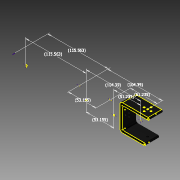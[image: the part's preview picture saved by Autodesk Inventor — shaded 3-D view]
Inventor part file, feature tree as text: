
AUTODESK INVENTOR PART (.ipt)
format: ipt  version: 2014 SP2 (Build 180246200, 246)  size: 362,496 bytes
history: native  units: in
note: dims shown in document units (in); Inventor stores cm internally (conversion verified against a paired STEP export)
features: sketch x18, extrude x13, reference x7, projected_geometry x5, mirror x4, pattern_circular x3, fillet x3, plane x2
ambient origin geometry x8: Origin, YZ Plane, XZ Plane, XY Plane, X Axis, Y Axis, Z Axis, Center Point
bodies: Solid1 (feature_tree)
feature tree (55):
  extrude  "Extrusion1"  Depth=0.1181in
  mirror  "Mirror1"
  mirror  "Mirror2"
  extrude  "Extrusion4"  Depth=2.126in
  mirror  "Mirror3"
  extrude  "Extrusion11"  Depth=0.1969in TaperAngle=0.0deg
  extrude  "Extrusion13"  Depth=0.0787in
  mirror  "Mirror4"
  extrude  "Extrusion14"  Depth=0.3937in
  pattern_circular  "Circular Pattern6"  Count=4 Angle=360.0deg
  extrude  "Extrusion15"  Depth=0.6299in
  pattern_circular  "Circular Pattern7"  Count=4 Angle=360.0deg
  extrude  "Extrusion16"  Depth=0.0787in
  plane  "Work Plane1"
  extrude  "Extrusion17"  Depth=0.1575in
  plane  "Work Plane3"
  extrude  "Extrusion18"  Depth=0.1181in
  sketch  "Sketch24"  dims[d78=0.5118in d79=0.6299in]
  extrude  "Extrusion22"  Depth=0.0591in
  sketch  "Sketch25"  dims[d80=0.1181in]
  extrude  "Extrusion23"  Depth=1.0236in
  extrude  "Extrusion24"  Depth=0.1969in TaperAngle=0.0deg
  pattern_circular  "Circular Pattern8"  [2 undecoded]
  extrude  "Extrusion25"  Depth=0.0787in TaperAngle=0.0deg
  fillet  "Fillet9"  Radius=0.1181in
  fillet  "Fillet10"  Radius=0.5118in
  fillet  "Fillet11"  Radius=0.1181in
  sketch  "Sketch29"  dims[d93=1.5748in d94=0.0in d95=0.1575in]
  sketch  "Sketch30"  dims[d96=1.378in d97=0.0in d110=0.1181in]
  sketch  "Sketch31"  dims[d111=0.0787in d112=0.0591in]
  sketch  "Sketch32"  dims[d113=0.0984in d114=1.0236in d115=3.0807in d116=0.0in d117=0.1181in d118=0.0787in d119=0.0in d120=0.1181in d121=0.5118in d122=0.1181in d123=0.6299in d124=0.3937in d125=0.0in d126=1.5748in d127=360.0deg d129=0.1575in d130=0.3937in d131=0.0in d132=0.0787in d133=0.1969in d134=0.1969in d135=2.0171in d136=4.1098in d137=2.0927in d138=2.0171in d139=4.1098in d140=2.0927in d141=4.5497in d142=4.5497in]
  sketch  "Sketch1"  dims[d0=0.7087in d1=0.1181in]
  sketch  "Sketch4"  dims[d2=0.1181in d3=2.126in]
  projected_geometry  "Projected Loop1"
  sketch  "Sketch11"  dims[d4=0.3937in d5=0.0in d16=0.1969in d17=0.0in]
  projected_geometry  "Projected Loop3"
  sketch  "Sketch13"  dims[d54=0.3937in d55=0.0in d65=0.0787in]
  sketch  "Sketch14"  dims[d66=0.3937in d67=0.0in d68=0.5118in]
  sketch  "Sketch15"  dims[d69=0.8661in]
  sketch  "Sketch16"  dims[d71=0.1181in]
  projected_geometry  "Projected Loop4"
  sketch  "Sketch17"  dims[d72=0.1181in]
  sketch  "Sketch18"  dims[d73=0.3937in d74=0.0in d75=1.5748in d76=360.0deg]
  projected_geometry  "Projected Loop5"
  sketch  "Sketch26"  dims[d81=0.1181in]
  projected_geometry  "Projected Loop6"
  sketch  "Sketch27"  dims[d82=0.3937in d83=0.0in d84=1.5748in d85=360.0deg]
  sketch  "Sketch28"  dims[d90=0.5512in d91=0.0in d92=0.0787in]
  reference  "Reference6"
  reference  "Reference7"
  reference  "Reference8"
  reference  "Reference9"
  reference  "Reference10"
  reference  "Reference11"
  reference  "Reference12"
note: 2 required parameter values undecoded (feature->parameter linkage not recoverable at this tier; creation-order binding heuristic only, values carry confidence <= 0.55)
